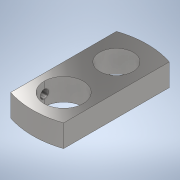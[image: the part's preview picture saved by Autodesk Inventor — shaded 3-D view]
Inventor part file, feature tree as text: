
AUTODESK INVENTOR PART (.ipt)
format: ipt  version: 2020 (Build 240168000, 168)  size: 133,120 bytes
history: native  units: mm
features: sketch x3, hole x3, extrude x1
ambient origin geometry x8: Origin, YZ Plane, XZ Plane, XY Plane, X Axis, Y Axis, Z Axis, Center Point
bodies: Solid1 (feature_tree)
feature tree (7):
  extrude  "Extrusion1"  Depth=19.0mm
  sketch  "Sketch2"  dims[d2=15.0mm d3=15.0mm]
  hole  "Hole1"  [1 undecoded]
  hole  "Hole2"  [1 undecoded]
  hole  "Hole3"  [1 undecoded]
  sketch  "Sketch1"  dims[d0=9.5mm d1=19.0mm]
  sketch  "Sketch3"  dims[d4=4.0mm d5=0.0mm d6=4.75mm d7=9.5mm d8=6.0mm d9=6.0mm d10=4.0mm d11=2.0mm d12=90.0deg d13=4.42mm d14=20.594885mm d15=7.0mm d16=6.0mm d17=4.0mm d18=2.0mm d19=90.0deg d20=4.42mm d21=20.594885mm d22=4.75mm d23=2.0mm d24=1.5mm d25=6.0mm d26=4.0mm d27=2.0mm d28=90.0deg d29=1.33mm d30=20.594885mm]
note: 3 required parameter values undecoded (feature->parameter linkage not recoverable at this tier; creation-order binding heuristic only, values carry confidence <= 0.55)
